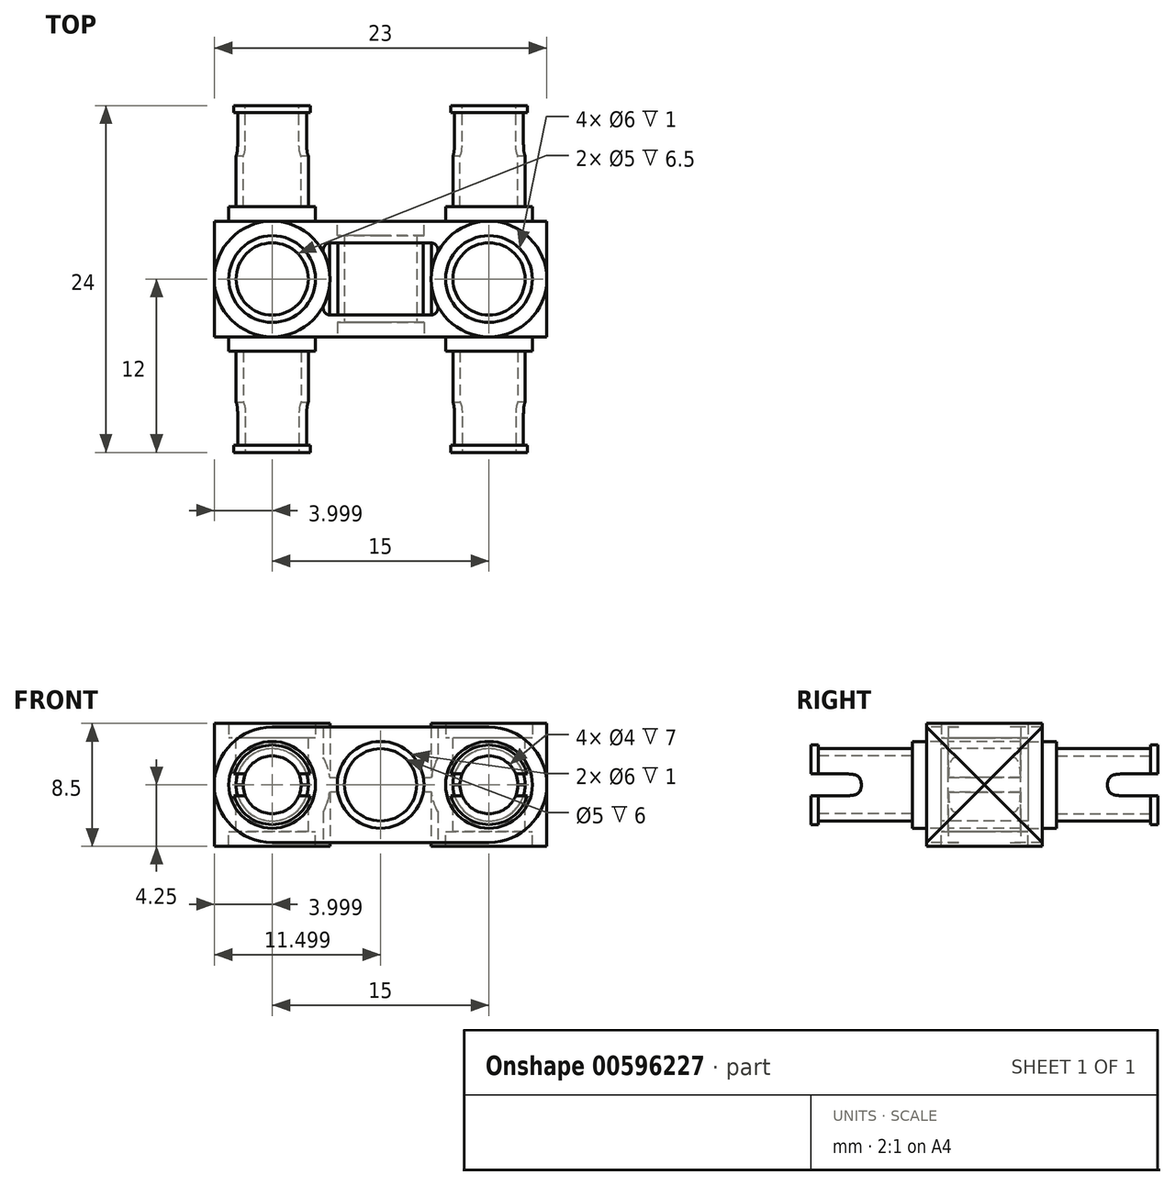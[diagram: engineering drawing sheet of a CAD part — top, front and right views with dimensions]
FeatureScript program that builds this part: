
annotation { "Feature Type Name" : "Feature", "Feature Type Description" : "" }
export const myFeature = defineFeature(function(context is Context, id is Id, definition is map)
    precondition{}
    {
        {
            var Q0;
            Q0=qCreatedBy(makeId("Top.planeOp"),FACE);
            var sketch = newSketch(context, id + "F0", { "sketchPlane" : qUnion([Q0])});
            skArc(sketch, "E0", {"start": v(-16.77, -19.7) * mm, "mid": v(-17.2, -21.48) * mm, "end": v(-16.77, -23.26) * mm});
            skArc(sketch, "E1", {"start": v(-24.6, -23.26) * mm, "mid": v(-24.2, -21.48) * mm, "end": v(-24.6, -19.7) * mm});
            skLineSegment(sketch, "E2", {"start": v(-28.2, -25.48) * mm, "end": v(-13.2, -25.48) * mm});
            skLineSegment(sketch, "E3", {"start": v(-28.2, -17.48) * mm, "end": v(-13.2, -17.48) * mm});
            skLineSegment(sketch, "E4", {"start": v(-17.22, -23.98) * mm, "end": v(-24.16, -23.98) * mm});
            skLineSegment(sketch, "E5", {"start": v(-17.22, -18.98) * mm, "end": v(-24.16, -18.98) * mm});
            skArc(sketch, "E6.trimOffspring", {"start": v(-28.2, -17.48) * mm, "mid": v(-32.2, -21.48) * mm, "end": v(-28.2, -25.48) * mm});
            skArc(sketch, "E7.trimOffspring", {"start": v(-13.2, -25.48) * mm, "mid": v(-9.2, -21.48) * mm, "end": v(-13.2, -17.48) * mm});
            skPoint(sketch, "E8.visualSharp", {"position": v(-25.07, -23.98) * mm});
            skArc(sketch, "E8.filletArc", {"start": v(-24.6, -23.26) * mm, "mid": v(-24.58, -23.74) * mm, "end": v(-24.16, -23.98) * mm});
            skPoint(sketch, "E9.visualSharp", {"position": v(-16.31, -23.98) * mm});
            skArc(sketch, "E9.filletArc", {"start": v(-17.22, -23.98) * mm, "mid": v(-16.8, -23.74) * mm, "end": v(-16.77, -23.26) * mm});
            skPoint(sketch, "E10.visualSharp", {"position": v(-16.31, -18.98) * mm});
            skArc(sketch, "E10.filletArc", {"start": v(-16.77, -19.7) * mm, "mid": v(-16.8, -19.22) * mm, "end": v(-17.22, -18.98) * mm});
            skPoint(sketch, "E11.visualSharp", {"position": v(-25.07, -18.98) * mm});
            skArc(sketch, "E11.filletArc", {"start": v(-24.16, -18.98) * mm, "mid": v(-24.58, -19.22) * mm, "end": v(-24.6, -19.7) * mm});
            skSolve(sketch);
        }
        {
            var Q0;
            Q0=makeQuery(id+"F0.imprint","IMPRINT",FACE,{"disambiguationData":[TD([[makeQuery(id+"F0.imprint","IMPRINT",EDGE,{"derivedFrom":sQuery(id+"F0.wireOp",EDGE,"E1")}),1.0]])]});
            var Q1;
            Q1=makeQuery(id+"F0.imprint","IMPRINT",FACE,{"disambiguationData":[TD([[makeQuery(id+"F0.imprint","IMPRINT",EDGE,{"derivedFrom":sQuery(id+"F0.wireOp",EDGE,"E0")}),1.0]])]});
            var Q2;
            {var subQ0=sQuery(id+"F0.wireOp",EDGE,"E2");Q2=makeQuery(id+"F0.imprint","IMPRINT",FACE,{"disambiguationData":[TD([[makeQuery(id+"F0.imprint","IMPRINT",EDGE,{"derivedFrom":subQ0}),1.0]])]});}
            var Q3;
            {var subQ0=sQuery(id+"F0.wireOp",EDGE,"E3");Q3=makeQuery(id+"F0.imprint","IMPRINT",FACE,{"disambiguationData":[TD([[makeQuery(id+"F0.imprint","IMPRINT",EDGE,{"derivedFrom":subQ0}),-1.0]])]});}
            extrude(context, id + "F1", {"entities" : qUnion([Q0, Q1, Q2, Q3]), "depth" : 8 * mm, "offsetDistance" : 25 * mm});
        }
        {
            var Q0;
            Q0=makeQuery(id+"F1.opExtrude","SWEPT_FACE",FACE,{"disambiguationData":[OSD([sQuery(id+"F0.wireOp",EDGE,"E2")])]});
            var sketch = newSketch(context, id + "F2", { "sketchPlane" : qUnion([Q0])});
            skPoint(sketch, "E12.endSnap0", {"position": v(-13.2, 4) * mm});
            skCircle(sketch, "E13", {"center": v(-20.7, 4) * mm, "radius": 3 * mm});
            skCircle(sketch, "E14", {"center": v(-20.7, 4) * mm, "radius": 2.5 * mm});
            skSolve(sketch);
        }
        {
            var Q0;
            Q0=makeQuery(id+"F2.imprint","IMPRINT",FACE,{"disambiguationData":[TD([[makeQuery(id+"F2.imprint","IMPRINT",EDGE,{"derivedFrom":sQuery(id+"F2.wireOp",EDGE,"E13")}),1.0]])]});
            extrude(context, id + "F3", {"entities" : qUnion([Q0]), "operationType" : NewBodyOperationType.ADD, "oppositeDirection" : true, "depth" : 8 * mm, "offsetDistance" : 25 * mm});
        }
        {
            var Q0;
            Q0=makeQuery(id+"F2.imprint","IMPRINT",FACE,{"disambiguationData":[TD([[makeQuery(id+"F2.imprint","IMPRINT",EDGE,{"derivedFrom":sQuery(id+"F2.wireOp",EDGE,"E14")}),1.0]])]});
            extrude(context, id + "F4", {"entities" : qUnion([Q0]), "operationType" : NewBodyOperationType.REMOVE, "oppositeDirection" : true, "depth" : 25 * mm, "offsetDistance" : 25 * mm});
        }
        {
            var Q0;
            Q0=makeQuery(id+"F2.imprint","IMPRINT",FACE,{"disambiguationData":[TD([[makeQuery(id+"F2.imprint","IMPRINT",EDGE,{"derivedFrom":sQuery(id+"F2.wireOp",EDGE,"E13")}),1.0]])]});
            extrude(context, id + "F5", {"entities" : qUnion([Q0]), "operationType" : NewBodyOperationType.REMOVE, "oppositeDirection" : true, "depth" : 1 * mm, "offsetDistance" : 25 * mm});
        }
        {
            var Q0;
            Q0=makeQuery(id+"F1.opExtrude","SWEPT_FACE",FACE,{"disambiguationData":[OSD([sQuery(id+"F0.wireOp",EDGE,"E3")])]});
            var sketch = newSketch(context, id + "F6", { "sketchPlane" : qUnion([Q0])});
            skCircle(sketch, "E15", {"center": v(20.7, 4) * mm, "radius": 3 * mm});
            skSolve(sketch);
        }
        {
            var Q0;
            Q0=makeQuery(id+"F6.imprint","IMPRINT",FACE,{"disambiguationData":[TD([[makeQuery(id+"F6.imprint","IMPRINT",EDGE,{"derivedFrom":sQuery(id+"F6.wireOp",EDGE,"E15")}),1.0]])]});
            extrude(context, id + "F7", {"entities" : qUnion([Q0]), "operationType" : NewBodyOperationType.REMOVE, "oppositeDirection" : true, "depth" : 1 * mm, "offsetDistance" : 25 * mm});
        }
        {
            var Q0;
            Q0=makeQuery(id+"F1.opExtrude","SWEPT_FACE",FACE,{"disambiguationData":[OSD([sQuery(id+"F0.wireOp",EDGE,"E3")])]});
            var sketch = newSketch(context, id + "F8", { "sketchPlane" : qUnion([Q0])});
            skCircle(sketch, "E16", {"center": v(13.2, 4) * mm, "radius": 4 * mm});
            skCircle(sketch, "E17", {"center": v(28.2, 4) * mm, "radius": 4 * mm});
            skSolve(sketch);
        }
        {
            var Q0;
            {var subQ1=sQuery(id+"F0.wireOp",EDGE,"E3");var subQ2=makeQuery(id+"F1.opExtrude","SWEPT_EDGE",EDGE,{"disambiguationData":[OSD([subQ1,sQuery(id+"F0.wireOp",EDGE,"E7.trimOffspring")])]});Q0=makeQuery(id+"F8.imprint","IMPRINT",FACE,{"disambiguationData":[TD([[makeQuery(id+"F8.imprint","IMPRINT",EDGE,{"derivedFrom":subQ2}),1.0]])]});}
            var Q1;
            {var subQ1=sQuery(id+"F0.wireOp",EDGE,"E3");var subQ2=makeQuery(id+"F1.opExtrude","SWEPT_EDGE",EDGE,{"disambiguationData":[OSD([subQ1,sQuery(id+"F0.wireOp",EDGE,"E7.trimOffspring")])]});Q1=makeQuery(id+"F8.imprint","IMPRINT",FACE,{"disambiguationData":[TD([[makeQuery(id+"F8.imprint","IMPRINT",EDGE,{"derivedFrom":subQ2}),-1.0]])]});}
            var Q2;
            {var subQ1=sQuery(id+"F0.wireOp",EDGE,"E3");var subQ2=makeQuery(id+"F1.opExtrude","SWEPT_EDGE",EDGE,{"disambiguationData":[OSD([subQ1,sQuery(id+"F0.wireOp",EDGE,"E6.trimOffspring")])]});Q2=makeQuery(id+"F8.imprint","IMPRINT",FACE,{"disambiguationData":[TD([[makeQuery(id+"F8.imprint","IMPRINT",EDGE,{"derivedFrom":subQ2}),-1.0]])]});}
            var Q3;
            {var subQ1=sQuery(id+"F0.wireOp",EDGE,"E3");var subQ2=makeQuery(id+"F1.opExtrude","SWEPT_EDGE",EDGE,{"disambiguationData":[OSD([subQ1,sQuery(id+"F0.wireOp",EDGE,"E6.trimOffspring")])]});Q3=makeQuery(id+"F8.imprint","IMPRINT",FACE,{"disambiguationData":[TD([[makeQuery(id+"F8.imprint","IMPRINT",EDGE,{"derivedFrom":subQ2}),1.0]])]});}
            extrude(context, id + "F9", {"entities" : qUnion([Q0, Q1, Q2, Q3]), "operationType" : NewBodyOperationType.ADD, "oppositeDirection" : true, "depth" : 16 * mm, "offsetDistance" : 25 * mm});
        }
        {
            var Q0;
            {var subQ1=sQuery(id+"F0.wireOp",EDGE,"E3");var subQ2=makeQuery(id+"F1.opExtrude","SWEPT_EDGE",EDGE,{"disambiguationData":[OSD([subQ1,sQuery(id+"F0.wireOp",EDGE,"E7.trimOffspring")])]});Q0=makeQuery(id+"F8.imprint","IMPRINT",FACE,{"disambiguationData":[TD([[makeQuery(id+"F8.imprint","IMPRINT",EDGE,{"derivedFrom":subQ2}),1.0]])]});}
            var Q1;
            {var subQ1=sQuery(id+"F0.wireOp",EDGE,"E3");var subQ2=makeQuery(id+"F1.opExtrude","SWEPT_EDGE",EDGE,{"disambiguationData":[OSD([subQ1,sQuery(id+"F0.wireOp",EDGE,"E7.trimOffspring")])]});Q1=makeQuery(id+"F8.imprint","IMPRINT",FACE,{"disambiguationData":[TD([[makeQuery(id+"F8.imprint","IMPRINT",EDGE,{"derivedFrom":subQ2}),-1.0]])]});}
            var Q2;
            {var subQ1=sQuery(id+"F0.wireOp",EDGE,"E3");var subQ2=makeQuery(id+"F1.opExtrude","SWEPT_EDGE",EDGE,{"disambiguationData":[OSD([subQ1,sQuery(id+"F0.wireOp",EDGE,"E6.trimOffspring")])]});Q2=makeQuery(id+"F8.imprint","IMPRINT",FACE,{"disambiguationData":[TD([[makeQuery(id+"F8.imprint","IMPRINT",EDGE,{"derivedFrom":subQ2}),-1.0]])]});}
            var Q3;
            {var subQ1=sQuery(id+"F0.wireOp",EDGE,"E3");var subQ2=makeQuery(id+"F1.opExtrude","SWEPT_EDGE",EDGE,{"disambiguationData":[OSD([subQ1,sQuery(id+"F0.wireOp",EDGE,"E6.trimOffspring")])]});Q3=makeQuery(id+"F8.imprint","IMPRINT",FACE,{"disambiguationData":[TD([[makeQuery(id+"F8.imprint","IMPRINT",EDGE,{"derivedFrom":subQ2}),1.0]])]});}
            extrude(context, id + "F10", {"entities" : qUnion([Q0, Q1, Q2, Q3]), "operationType" : NewBodyOperationType.ADD, "depth" : 8 * mm, "offsetDistance" : 25 * mm});
        }
        {
            var Q0;
            Q0=makeQuery(id+"F10.opExtrude","CAP_FACE",FACE,{"disambiguationData":[OSD([sQuery(id+"F8.wireOp",EDGE,"E16")])],"isStart":false});
            var sketch = newSketch(context, id + "F11", { "sketchPlane" : qUnion([Q0])});
            skCircle(sketch, "E18", {"center": v(13.2, 4) * mm, "radius": 3 * mm});
            skCircle(sketch, "E19", {"center": v(13.2, 4) * mm, "radius": 2.5 * mm});
            skSolve(sketch);
        }
        {
            var Q0;
            Q0=makeQuery(id+"F11.imprint","IMPRINT",FACE,{"disambiguationData":[TD([[makeQuery(id+"F11.imprint","IMPRINT",EDGE,{"derivedFrom":sQuery(id+"F11.wireOp",EDGE,"E18")}),-1.0]])]});
            extrude(context, id + "F12", {"entities" : qUnion([Q0]), "operationType" : NewBodyOperationType.REMOVE, "oppositeDirection" : true, "depth" : 8 * mm, "offsetDistance" : 25 * mm});
        }
        {
            var Q0;
            Q0=makeQuery(id+"F11.imprint","IMPRINT",FACE,{"disambiguationData":[TD([[makeQuery(id+"F11.imprint","IMPRINT",EDGE,{"derivedFrom":sQuery(id+"F11.wireOp",EDGE,"E18")}),1.0]])]});
            extrude(context, id + "F13", {"entities" : qUnion([Q0]), "operationType" : NewBodyOperationType.REMOVE, "oppositeDirection" : true, "depth" : 7 * mm, "offsetDistance" : 25 * mm});
        }
        {
            var Q0;
            Q0=makeQuery(id+"F10.opExtrude","CAP_FACE",FACE,{"disambiguationData":[OSD([sQuery(id+"F8.wireOp",EDGE,"E16")])],"isStart":false});
            var sketch = newSketch(context, id + "F14", { "sketchPlane" : qUnion([Q0])});
            skCircle(sketch, "E20", {"center": v(13.2, 4) * mm, "radius": 2.75 * mm});
            skSolve(sketch);
        }
        {
            var Q0;
            Q0=makeQuery(id+"F14.imprint","IMPRINT",FACE,{"disambiguationData":[TD([[makeQuery(id+"F14.imprint","IMPRINT",EDGE,{"derivedFrom":sQuery(id+"F14.wireOp",EDGE,"E20")}),1.0]])]});
            extrude(context, id + "F15", {"entities" : qUnion([Q0]), "operationType" : NewBodyOperationType.ADD, "oppositeDirection" : true, "depth" : .5 * mm, "offsetDistance" : 25 * mm});
        }
        {
            var Q0;
            Q0=makeQuery(id+"F15.boolean.opBoolean","MERGE",FACE,{"derivedFrom":[makeQuery(id+"F10.opExtrude","CAP_FACE",FACE,{"disambiguationData":[OSD([sQuery(id+"F8.wireOp",EDGE,"E16")])],"isStart":false}),makeQuery(id+"F15.opExtrude","CAP_FACE",FACE,{"disambiguationData":[OSD([sQuery(id+"F11.wireOp",EDGE,"E19"),sQuery(id+"F14.wireOp",EDGE,"E20")])],"isStart":true})]});
            var sketch = newSketch(context, id + "F16", { "sketchPlane" : qUnion([Q0])});
            skCircle(sketch, "E21", {"center": v(13.2, 4) * mm, "radius": 2 * mm});
            skSolve(sketch);
        }
        {
            var Q0;
            Q0=makeQuery(id+"F16.imprint","IMPRINT",FACE,{"disambiguationData":[TD([[makeQuery(id+"F16.imprint","IMPRINT",EDGE,{"derivedFrom":sQuery(id+"F16.wireOp",EDGE,"E21")}),1.0]])]});
            extrude(context, id + "F17", {"entities" : qUnion([Q0]), "operationType" : NewBodyOperationType.REMOVE, "oppositeDirection" : true, "depth" : 7 * mm, "offsetDistance" : 25 * mm});
        }
        {
            var Q0;
            Q0=makeQuery(id+"F10.opExtrude","CAP_FACE",FACE,{"disambiguationData":[OSD([sQuery(id+"F8.wireOp",EDGE,"E17")])],"isStart":false});
            var sketch = newSketch(context, id + "F18", { "sketchPlane" : qUnion([Q0])});
            skCircle(sketch, "E22", {"center": v(28.2, 4) * mm, "radius": 3 * mm});
            skCircle(sketch, "E23", {"center": v(28.2, 4) * mm, "radius": 2.5 * mm});
            skCircle(sketch, "E24", {"center": v(28.2, 4) * mm, "radius": 2 * mm});
            skSolve(sketch);
        }
        {
            var Q0;
            Q0=makeQuery(id+"F18.imprint","IMPRINT",FACE,{"disambiguationData":[TD([[makeQuery(id+"F18.imprint","IMPRINT",EDGE,{"derivedFrom":sQuery(id+"F18.wireOp",EDGE,"E22")}),-1.0]])]});
            extrude(context, id + "F19", {"entities" : qUnion([Q0]), "operationType" : NewBodyOperationType.REMOVE, "oppositeDirection" : true, "depth" : 8 * mm, "offsetDistance" : 25 * mm});
        }
        {
            var Q0;
            Q0=makeQuery(id+"F18.imprint","IMPRINT",FACE,{"disambiguationData":[TD([[makeQuery(id+"F18.imprint","IMPRINT",EDGE,{"derivedFrom":sQuery(id+"F18.wireOp",EDGE,"E22")}),1.0]])]});
            extrude(context, id + "F20", {"entities" : qUnion([Q0]), "operationType" : NewBodyOperationType.REMOVE, "oppositeDirection" : true, "depth" : 7 * mm, "offsetDistance" : 25 * mm});
        }
        {
            var Q0;
            Q0=makeQuery(id+"F18.imprint","IMPRINT",FACE,{"disambiguationData":[TD([[makeQuery(id+"F18.imprint","IMPRINT",EDGE,{"derivedFrom":sQuery(id+"F18.wireOp",EDGE,"E24")}),1.0]])]});
            extrude(context, id + "F21", {"entities" : qUnion([Q0]), "operationType" : NewBodyOperationType.REMOVE, "oppositeDirection" : true, "depth" : 7 * mm, "offsetDistance" : 25 * mm});
        }
        {
            var Q0;
            Q0=makeQuery(id+"F10.opExtrude","CAP_FACE",FACE,{"disambiguationData":[OSD([sQuery(id+"F8.wireOp",EDGE,"E17")])],"isStart":false});
            var sketch = newSketch(context, id + "F22", { "sketchPlane" : qUnion([Q0])});
            skCircle(sketch, "E25", {"center": v(28.2, 4) * mm, "radius": 2.75 * mm});
            skSolve(sketch);
        }
        {
            var Q0;
            Q0=makeQuery(id+"F22.imprint","IMPRINT",FACE,{"disambiguationData":[TD([[makeQuery(id+"F22.imprint","IMPRINT",EDGE,{"derivedFrom":sQuery(id+"F22.wireOp",EDGE,"E25")}),1.0]])]});
            extrude(context, id + "F23", {"entities" : qUnion([Q0]), "operationType" : NewBodyOperationType.ADD, "oppositeDirection" : true, "depth" : .5 * mm, "offsetDistance" : 25 * mm});
        }
        {
            var Q0;
            Q0=makeQuery(id+"F23.boolean.opBoolean","MERGE",FACE,{"derivedFrom":[makeQuery(id+"F10.opExtrude","CAP_FACE",FACE,{"disambiguationData":[OSD([sQuery(id+"F8.wireOp",EDGE,"E17")])],"isStart":false}),makeQuery(id+"F23.opExtrude","CAP_FACE",FACE,{"disambiguationData":[OSD([sQuery(id+"F18.wireOp",EDGE,"E23"),sQuery(id+"F22.wireOp",EDGE,"E25")])],"isStart":true})]});
            var sketch = newSketch(context, id + "F24", { "sketchPlane" : qUnion([Q0])});
            skLineSegment(sketch, "E26", {"start": v(13.2, 4) * mm, "end": v(13.2, 4.75) * mm});
            skLineSegment(sketch, "E27", {"start": v(13.2, 4.75) * mm, "end": v(36.7, 4.75) * mm});
            skLineSegment(sketch, "E28", {"start": v(36.7, 4.75) * mm, "end": v(36.7, 3.25) * mm});
            skLineSegment(sketch, "E29", {"start": v(36.7, 3.25) * mm, "end": v(7.51, 3.25) * mm});
            skLineSegment(sketch, "E30", {"start": v(7.51, 3.25) * mm, "end": v(7.51, 4.75) * mm});
            skLineSegment(sketch, "E31", {"start": v(7.51, 4.75) * mm, "end": v(13.2, 4.75) * mm});
            skSolve(sketch);
        }
        {
            var Q0;
            {var subQ1=sQuery(id+"F24.wireOp",EDGE,"E30");Q0=makeQuery(id+"F24.imprint","IMPRINT",FACE,{"disambiguationData":[TD([[makeQuery(id+"F24.imprint","IMPRINT",EDGE,{"derivedFrom":subQ1}),-1.0]])]});}
            var Q1;
            {var subQ0=sQuery(id+"F24.wireOp",EDGE,"E27");var subQ1=makeQuery(id+"F23.opExtrude","CAP_EDGE",EDGE,{"disambiguationData":[OSD([sQuery(id+"F22.wireOp",EDGE,"E25")])],"isStart":true});var subQ2=makeQuery(id+"F24.imprint","INTERSECT",VERTEX,{"disambiguationData":[OD(1.0)],"derivedFrom":[subQ1,subQ0]});Q1=makeQuery(id+"F24.imprint","IMPRINT",FACE,{"disambiguationData":[TD([[makeQuery(id+"F24.imprint","IMPRINT",EDGE,{"disambiguationData":[TD([[subQ2,1.0]])],"derivedFrom":subQ0}),-1.0]])]});}
            var Q2;
            {var subQ0=sQuery(id+"F24.wireOp",EDGE,"E27");var subQ1=makeQuery(id+"F23.opExtrude","CAP_EDGE",EDGE,{"disambiguationData":[OSD([sQuery(id+"F22.wireOp",EDGE,"E25")])],"isStart":true});var subQ2=makeQuery(id+"F24.imprint","INTERSECT",VERTEX,{"disambiguationData":[OD(0.0)],"derivedFrom":[subQ1,subQ0]});Q2=makeQuery(id+"F24.imprint","IMPRINT",FACE,{"disambiguationData":[TD([[makeQuery(id+"F24.imprint","IMPRINT",EDGE,{"disambiguationData":[TD([[subQ2,-1.0]])],"derivedFrom":subQ0}),-1.0]])]});}
            extrude(context, id + "F25", {"entities" : qUnion([Q0, Q1, Q2]), "operationType" : NewBodyOperationType.REMOVE, "oppositeDirection" : true, "depth" : 3.5 * mm, "offsetDistance" : 25 * mm});
        }
        {
            var Q0;
            {var subQ0=sQuery(id+"F24.wireOp",EDGE,"E31");var subQ1=sQuery(id+"F24.wireOp",EDGE,"E27");Q0=makeQuery(id+"F25.boolean.opBoolean","COPY",EDGE,{"disambiguationData":[TD([makeQuery(id+"F13.boolean.opBoolean","COPY",FACE,{"derivedFrom":makeQuery(id+"F13.opExtrude","SWEPT_FACE",FACE,{"disambiguationData":[OSD([sQuery(id+"F11.wireOp",EDGE,"E19")])]})}),makeQuery(id+"F17.boolean.opBoolean","COPY",FACE,{"derivedFrom":makeQuery(id+"F17.opExtrude","SWEPT_FACE",FACE,{"disambiguationData":[OSD([sQuery(id+"F16.wireOp",EDGE,"E21")])]})}),makeQuery(id+"F25.opExtrude","CAP_FACE",FACE,{"disambiguationData":[OSD([sQuery(id+"F18.wireOp",EDGE,"E24"),subQ1,sQuery(id+"F24.wireOp",EDGE,"E29"),sQuery(id+"F24.wireOp",EDGE,"E30"),subQ0])],"isStart":false}),makeQuery(id+"F25.opExtrude","SWEPT_FACE",FACE,{"disambiguationData":[OSD([subQ1,subQ0])]})]),OD(1.0)],"derivedFrom":makeQuery(id+"F25.opExtrude","CAP_EDGE",EDGE,{"disambiguationData":[OSD([subQ1,subQ0])],"isStart":false})});}
            var Q1;
            {var subQ0=sQuery(id+"F24.wireOp",EDGE,"E30");var subQ1=sQuery(id+"F24.wireOp",EDGE,"E29");var subQ2=sQuery(id+"F18.wireOp",EDGE,"E24");var subQ3=makeQuery(id+"F24.imprint","INTERSECT",VERTEX,{"disambiguationData":[OD(1.0)],"derivedFrom":[makeQuery(id+"F23.opExtrude","CAP_EDGE",EDGE,{"disambiguationData":[OSD([sQuery(id+"F22.wireOp",EDGE,"E25")])],"isStart":true}),subQ1]});var subQ4=makeQuery(id+"F24.imprint","IMPRINT",EDGE,{"disambiguationData":[TD([[makeQuery(id+"F24.imprint","INTERSECT",VERTEX,{"derivedFrom":[subQ1,subQ0]}),1.0]])],"derivedFrom":subQ1});var subQ5=makeQuery(id+"F24.imprint","IMPRINT",EDGE,{"disambiguationData":[TD([[subQ3,1.0]])],"derivedFrom":subQ1});Q1=makeQuery(id+"F25.boolean.opBoolean","COPY",EDGE,{"disambiguationData":[TD([makeQuery(id+"F13.boolean.opBoolean","COPY",FACE,{"derivedFrom":makeQuery(id+"F13.opExtrude","SWEPT_FACE",FACE,{"disambiguationData":[OSD([sQuery(id+"F11.wireOp",EDGE,"E19")])]})}),makeQuery(id+"F17.boolean.opBoolean","COPY",FACE,{"derivedFrom":makeQuery(id+"F17.opExtrude","SWEPT_FACE",FACE,{"disambiguationData":[OSD([sQuery(id+"F16.wireOp",EDGE,"E21")])]})}),makeQuery(id+"F25.opExtrude","CAP_FACE",FACE,{"disambiguationData":[OSD([subQ2,sQuery(id+"F24.wireOp",EDGE,"E27"),subQ1,subQ0,sQuery(id+"F24.wireOp",EDGE,"E31")])],"isStart":false}),makeQuery(id+"F25.opExtrude","SWEPT_FACE",FACE,{"disambiguationData":[OSD([subQ1]),TDD([subQ5,subQ4])]})]),OD(1.0)],"derivedFrom":makeQuery(id+"F25.opExtrude","CAP_EDGE",EDGE,{"disambiguationData":[OSD([subQ1]),TDD([subQ5,subQ4])],"isStart":false})});}
            var Q2;
            {var subQ0=sQuery(id+"F24.wireOp",EDGE,"E30");var subQ1=sQuery(id+"F24.wireOp",EDGE,"E29");var subQ2=sQuery(id+"F18.wireOp",EDGE,"E24");var subQ3=makeQuery(id+"F24.imprint","INTERSECT",VERTEX,{"disambiguationData":[OD(1.0)],"derivedFrom":[makeQuery(id+"F23.opExtrude","CAP_EDGE",EDGE,{"disambiguationData":[OSD([sQuery(id+"F22.wireOp",EDGE,"E25")])],"isStart":true}),subQ1]});var subQ4=makeQuery(id+"F24.imprint","IMPRINT",EDGE,{"disambiguationData":[TD([[makeQuery(id+"F24.imprint","INTERSECT",VERTEX,{"derivedFrom":[subQ1,subQ0]}),1.0]])],"derivedFrom":subQ1});var subQ5=makeQuery(id+"F24.imprint","IMPRINT",EDGE,{"disambiguationData":[TD([[subQ3,1.0]])],"derivedFrom":subQ1});Q2=makeQuery(id+"F25.boolean.opBoolean","COPY",EDGE,{"disambiguationData":[TD([makeQuery(id+"F13.boolean.opBoolean","COPY",FACE,{"derivedFrom":makeQuery(id+"F13.opExtrude","SWEPT_FACE",FACE,{"disambiguationData":[OSD([sQuery(id+"F11.wireOp",EDGE,"E19")])]})}),makeQuery(id+"F17.boolean.opBoolean","COPY",FACE,{"derivedFrom":makeQuery(id+"F17.opExtrude","SWEPT_FACE",FACE,{"disambiguationData":[OSD([sQuery(id+"F16.wireOp",EDGE,"E21")])]})}),makeQuery(id+"F25.opExtrude","CAP_FACE",FACE,{"disambiguationData":[OSD([subQ2,sQuery(id+"F24.wireOp",EDGE,"E27"),subQ1,subQ0,sQuery(id+"F24.wireOp",EDGE,"E31")])],"isStart":false}),makeQuery(id+"F25.opExtrude","SWEPT_FACE",FACE,{"disambiguationData":[OSD([subQ1]),TDD([subQ5,subQ4])]})]),OD(0.0)],"derivedFrom":makeQuery(id+"F25.opExtrude","CAP_EDGE",EDGE,{"disambiguationData":[OSD([subQ1]),TDD([subQ5,subQ4])],"isStart":false})});}
            var Q3;
            {var subQ0=sQuery(id+"F24.wireOp",EDGE,"E31");var subQ1=sQuery(id+"F24.wireOp",EDGE,"E27");Q3=makeQuery(id+"F25.boolean.opBoolean","COPY",EDGE,{"disambiguationData":[TD([makeQuery(id+"F13.boolean.opBoolean","COPY",FACE,{"derivedFrom":makeQuery(id+"F13.opExtrude","SWEPT_FACE",FACE,{"disambiguationData":[OSD([sQuery(id+"F11.wireOp",EDGE,"E19")])]})}),makeQuery(id+"F17.boolean.opBoolean","COPY",FACE,{"derivedFrom":makeQuery(id+"F17.opExtrude","SWEPT_FACE",FACE,{"disambiguationData":[OSD([sQuery(id+"F16.wireOp",EDGE,"E21")])]})}),makeQuery(id+"F25.opExtrude","CAP_FACE",FACE,{"disambiguationData":[OSD([sQuery(id+"F18.wireOp",EDGE,"E24"),subQ1,sQuery(id+"F24.wireOp",EDGE,"E29"),sQuery(id+"F24.wireOp",EDGE,"E30"),subQ0])],"isStart":false}),makeQuery(id+"F25.opExtrude","SWEPT_FACE",FACE,{"disambiguationData":[OSD([subQ1,subQ0])]})]),OD(0.0)],"derivedFrom":makeQuery(id+"F25.opExtrude","CAP_EDGE",EDGE,{"disambiguationData":[OSD([subQ1,subQ0])],"isStart":false})});}
            var Q4;
            Q4=makeQuery(id+"F25.boolean.opBoolean","COPY",EDGE,{"derivedFrom":makeQuery(id+"F25.opExtrude","CAP_EDGE",EDGE,{"disambiguationData":[OSD([sQuery(id+"F24.wireOp",EDGE,"E27")])],"isStart":false})});
            var Q5;
            {var subQ0=sQuery(id+"F24.wireOp",EDGE,"E31");var subQ1=sQuery(id+"F24.wireOp",EDGE,"E27");var subQ2=sQuery(id+"F18.wireOp",EDGE,"E24");Q5=makeQuery(id+"F25.boolean.opBoolean","COPY",EDGE,{"disambiguationData":[TD([makeQuery(id+"F20.boolean.opBoolean","COPY",FACE,{"derivedFrom":makeQuery(id+"F20.opExtrude","SWEPT_FACE",FACE,{"disambiguationData":[OSD([sQuery(id+"F18.wireOp",EDGE,"E23")])]})}),makeQuery(id+"F21.boolean.opBoolean","COPY",FACE,{"derivedFrom":makeQuery(id+"F21.opExtrude","SWEPT_FACE",FACE,{"disambiguationData":[OSD([subQ2])]})}),makeQuery(id+"F25.opExtrude","CAP_FACE",FACE,{"disambiguationData":[OSD([subQ2,subQ1,sQuery(id+"F24.wireOp",EDGE,"E29"),sQuery(id+"F24.wireOp",EDGE,"E30"),subQ0])],"isStart":false}),makeQuery(id+"F25.opExtrude","SWEPT_FACE",FACE,{"disambiguationData":[OSD([subQ1,subQ0])]})])],"derivedFrom":makeQuery(id+"F25.opExtrude","CAP_EDGE",EDGE,{"disambiguationData":[OSD([subQ1,subQ0])],"isStart":false})});}
            var Q6;
            {var subQ0=sQuery(id+"F24.wireOp",EDGE,"E30");var subQ1=sQuery(id+"F24.wireOp",EDGE,"E29");var subQ2=makeQuery(id+"F24.imprint","INTERSECT",VERTEX,{"disambiguationData":[OD(1.0)],"derivedFrom":[makeQuery(id+"F23.opExtrude","CAP_EDGE",EDGE,{"disambiguationData":[OSD([sQuery(id+"F22.wireOp",EDGE,"E25")])],"isStart":true}),subQ1]});var subQ3=makeQuery(id+"F24.imprint","IMPRINT",EDGE,{"disambiguationData":[TD([[makeQuery(id+"F24.imprint","INTERSECT",VERTEX,{"derivedFrom":[subQ1,subQ0]}),1.0]])],"derivedFrom":subQ1});var subQ4=sQuery(id+"F18.wireOp",EDGE,"E24");var subQ5=makeQuery(id+"F24.imprint","IMPRINT",EDGE,{"disambiguationData":[TD([[subQ2,1.0]])],"derivedFrom":subQ1});Q6=makeQuery(id+"F25.boolean.opBoolean","COPY",EDGE,{"disambiguationData":[TD([makeQuery(id+"F20.boolean.opBoolean","COPY",FACE,{"derivedFrom":makeQuery(id+"F20.opExtrude","SWEPT_FACE",FACE,{"disambiguationData":[OSD([sQuery(id+"F18.wireOp",EDGE,"E23")])]})}),makeQuery(id+"F21.boolean.opBoolean","COPY",FACE,{"derivedFrom":makeQuery(id+"F21.opExtrude","SWEPT_FACE",FACE,{"disambiguationData":[OSD([subQ4])]})}),makeQuery(id+"F25.opExtrude","CAP_FACE",FACE,{"disambiguationData":[OSD([subQ4,sQuery(id+"F24.wireOp",EDGE,"E27"),subQ1,subQ0,sQuery(id+"F24.wireOp",EDGE,"E31")])],"isStart":false}),makeQuery(id+"F25.opExtrude","SWEPT_FACE",FACE,{"disambiguationData":[OSD([subQ1]),TDD([subQ5,subQ3])]})])],"derivedFrom":makeQuery(id+"F25.opExtrude","CAP_EDGE",EDGE,{"disambiguationData":[OSD([subQ1]),TDD([subQ5,subQ3])],"isStart":false})});}
            var Q7;
            {var subQ0=sQuery(id+"F24.wireOp",EDGE,"E29");Q7=makeQuery(id+"F25.boolean.opBoolean","COPY",EDGE,{"derivedFrom":makeQuery(id+"F25.opExtrude","CAP_EDGE",EDGE,{"disambiguationData":[OSD([subQ0]),TDD([makeQuery(id+"F24.imprint","IMPRINT",EDGE,{"disambiguationData":[TD([[makeQuery(id+"F24.imprint","INTERSECT",VERTEX,{"disambiguationData":[OD(0.0)],"derivedFrom":[makeQuery(id+"F23.opExtrude","CAP_EDGE",EDGE,{"disambiguationData":[OSD([sQuery(id+"F22.wireOp",EDGE,"E25")])],"isStart":true}),subQ0]}),-1.0]])],"derivedFrom":subQ0})])],"isStart":false})});}
            fillet(context, id + "F26", {"entities" : qUnion([Q0, Q1, Q2, Q3, Q4, Q5, Q6, Q7]), "radius" : 1 * mm, "tangentPropagation" : true, "rho" : .6, "crossSection" : FilletCrossSection.CONIC, "allowEdgeOverflow" : false});
        }
        {
            var Q0;
            Q0=makeQuery(id+"F9.opExtrude","CAP_FACE",FACE,{"disambiguationData":[OSD([sQuery(id+"F8.wireOp",EDGE,"E17")])],"isStart":false});
            var sketch = newSketch(context, id + "F27", { "sketchPlane" : qUnion([Q0])});
            skCircle(sketch, "E32", {"center": v(-28.2, 4) * mm, "radius": 3 * mm});
            skCircle(sketch, "E33", {"center": v(-28.2, 4) * mm, "radius": 2.5 * mm});
            skCircle(sketch, "E34", {"center": v(-28.2, 4) * mm, "radius": 2.75 * mm});
            skCircle(sketch, "E35", {"center": v(-28.2, 4) * mm, "radius": 2 * mm});
            skSolve(sketch);
        }
        {
            var Q0;
            Q0=makeQuery(id+"F27.imprint","IMPRINT",FACE,{"disambiguationData":[TD([[makeQuery(id+"F27.imprint","IMPRINT",EDGE,{"derivedFrom":sQuery(id+"F27.wireOp",EDGE,"E32")}),-1.0]])]});
            extrude(context, id + "F28", {"entities" : qUnion([Q0]), "operationType" : NewBodyOperationType.REMOVE, "oppositeDirection" : true, "depth" : 8 * mm, "offsetDistance" : 25 * mm});
        }
        {
            var Q0;
            Q0=makeQuery(id+"F27.imprint","IMPRINT",FACE,{"disambiguationData":[TD([[makeQuery(id+"F27.imprint","IMPRINT",EDGE,{"derivedFrom":sQuery(id+"F27.wireOp",EDGE,"E33")}),-1.0]])]});
            var Q1;
            Q1=makeQuery(id+"F27.imprint","IMPRINT",FACE,{"disambiguationData":[TD([[makeQuery(id+"F27.imprint","IMPRINT",EDGE,{"derivedFrom":sQuery(id+"F27.wireOp",EDGE,"E32")}),1.0]])]});
            extrude(context, id + "F29", {"entities" : qUnion([Q0, Q1]), "operationType" : NewBodyOperationType.REMOVE, "oppositeDirection" : true, "depth" : 7 * mm, "offsetDistance" : 25 * mm});
        }
        {
            var Q0;
            Q0=makeQuery(id+"F27.imprint","IMPRINT",FACE,{"disambiguationData":[TD([[makeQuery(id+"F27.imprint","IMPRINT",EDGE,{"derivedFrom":sQuery(id+"F27.wireOp",EDGE,"E33")}),-1.0]])]});
            extrude(context, id + "F30", {"entities" : qUnion([Q0]), "operationType" : NewBodyOperationType.ADD, "oppositeDirection" : true, "depth" : .5 * mm, "offsetDistance" : 25 * mm});
        }
        {
            var Q0;
            Q0=makeQuery(id+"F27.imprint","IMPRINT",FACE,{"disambiguationData":[TD([[makeQuery(id+"F27.imprint","IMPRINT",EDGE,{"derivedFrom":sQuery(id+"F27.wireOp",EDGE,"E35")}),1.0]])]});
            extrude(context, id + "F31", {"entities" : qUnion([Q0]), "operationType" : NewBodyOperationType.REMOVE, "oppositeDirection" : true, "depth" : 7 * mm, "offsetDistance" : 25 * mm});
        }
        {
            var Q0;
            Q0=makeQuery(id+"F9.opExtrude","CAP_FACE",FACE,{"disambiguationData":[OSD([sQuery(id+"F8.wireOp",EDGE,"E16")])],"isStart":false});
            var sketch = newSketch(context, id + "F32", { "sketchPlane" : qUnion([Q0])});
            skCircle(sketch, "E36", {"center": v(-13.2, 4) * mm, "radius": 3 * mm});
            skCircle(sketch, "E37", {"center": v(-13.2, 4) * mm, "radius": 2.5 * mm});
            skCircle(sketch, "E38", {"center": v(-13.2, 4) * mm, "radius": 2 * mm});
            skSolve(sketch);
        }
        {
            var Q0;
            Q0=makeQuery(id+"F32.imprint","IMPRINT",FACE,{"disambiguationData":[TD([[makeQuery(id+"F32.imprint","IMPRINT",EDGE,{"derivedFrom":sQuery(id+"F32.wireOp",EDGE,"E36")}),-1.0]])]});
            extrude(context, id + "F33", {"entities" : qUnion([Q0]), "operationType" : NewBodyOperationType.REMOVE, "oppositeDirection" : true, "depth" : 8 * mm, "offsetDistance" : 25 * mm});
        }
        {
            var Q0;
            Q0=makeQuery(id+"F32.imprint","IMPRINT",FACE,{"disambiguationData":[TD([[makeQuery(id+"F32.imprint","IMPRINT",EDGE,{"derivedFrom":sQuery(id+"F32.wireOp",EDGE,"E36")}),1.0]])]});
            extrude(context, id + "F34", {"entities" : qUnion([Q0]), "operationType" : NewBodyOperationType.REMOVE, "oppositeDirection" : true, "depth" : 7 * mm, "offsetDistance" : 25 * mm});
        }
        {
            var Q0;
            Q0=makeQuery(id+"F32.imprint","IMPRINT",FACE,{"disambiguationData":[TD([[makeQuery(id+"F32.imprint","IMPRINT",EDGE,{"derivedFrom":sQuery(id+"F32.wireOp",EDGE,"E38")}),1.0]])]});
            extrude(context, id + "F35", {"entities" : qUnion([Q0]), "operationType" : NewBodyOperationType.REMOVE, "oppositeDirection" : true, "depth" : 7 * mm, "offsetDistance" : 25 * mm});
        }
        {
            var Q0;
            Q0=makeQuery(id+"F9.opExtrude","CAP_FACE",FACE,{"disambiguationData":[OSD([sQuery(id+"F8.wireOp",EDGE,"E16")])],"isStart":false});
            var sketch = newSketch(context, id + "F36", { "sketchPlane" : qUnion([Q0])});
            skCircle(sketch, "E39", {"center": v(-13.2, 4) * mm, "radius": 2.75 * mm});
            skSolve(sketch);
        }
        {
            var Q0;
            Q0=makeQuery(id+"F36.imprint","IMPRINT",FACE,{"disambiguationData":[TD([[makeQuery(id+"F36.imprint","IMPRINT",EDGE,{"derivedFrom":sQuery(id+"F36.wireOp",EDGE,"E39")}),1.0]])]});
            extrude(context, id + "F37", {"entities" : qUnion([Q0]), "operationType" : NewBodyOperationType.ADD, "oppositeDirection" : true, "depth" : .5 * mm, "offsetDistance" : 25 * mm});
        }
        {
            var Q0;
            Q0=makeQuery(id+"F37.boolean.opBoolean","MERGE",FACE,{"derivedFrom":[makeQuery(id+"F9.opExtrude","CAP_FACE",FACE,{"disambiguationData":[OSD([sQuery(id+"F8.wireOp",EDGE,"E16")])],"isStart":false}),makeQuery(id+"F37.opExtrude","CAP_FACE",FACE,{"disambiguationData":[OSD([sQuery(id+"F32.wireOp",EDGE,"E37"),sQuery(id+"F36.wireOp",EDGE,"E39")])],"isStart":true})]});
            var sketch = newSketch(context, id + "F38", { "sketchPlane" : qUnion([Q0])});
            skLineSegment(sketch, "E40", {"start": v(-13.2, 4) * mm, "end": v(-13.2, 4.75) * mm});
            skLineSegment(sketch, "E41", {"start": v(-13.2, 4.75) * mm, "end": v(-33.18, 4.75) * mm});
            skLineSegment(sketch, "E42", {"start": v(-33.18, 4.75) * mm, "end": v(-33.18, 3.25) * mm});
            skLineSegment(sketch, "E43", {"start": v(-33.18, 3.25) * mm, "end": v(-4.02, 3.25) * mm});
            skLineSegment(sketch, "E44", {"start": v(-4.02, 3.25) * mm, "end": v(-4.02, 4.75) * mm});
            skLineSegment(sketch, "E45", {"start": v(-4.02, 4.75) * mm, "end": v(-13.2, 4.75) * mm});
            skSolve(sketch);
        }
        {
            var Q0;
            {var subQ0=sQuery(id+"F38.wireOp",EDGE,"E41");var subQ1=makeQuery(id+"F37.opExtrude","CAP_EDGE",EDGE,{"disambiguationData":[OSD([sQuery(id+"F36.wireOp",EDGE,"E39")])],"isStart":true});var subQ2=makeQuery(id+"F38.imprint","INTERSECT",VERTEX,{"derivedFrom":[subQ1,subQ0]});Q0=makeQuery(id+"F38.imprint","IMPRINT",FACE,{"disambiguationData":[TD([[makeQuery(id+"F38.imprint","IMPRINT",EDGE,{"disambiguationData":[TD([[subQ2,1.0]])],"derivedFrom":subQ0}),1.0]])]});}
            var Q1;
            {var subQ0=sQuery(id+"F38.wireOp",EDGE,"E43");var subQ1=makeQuery(id+"F37.opExtrude","CAP_EDGE",EDGE,{"disambiguationData":[OSD([sQuery(id+"F36.wireOp",EDGE,"E39")])],"isStart":true});var subQ2=makeQuery(id+"F38.imprint","INTERSECT",VERTEX,{"disambiguationData":[OD(1.0)],"derivedFrom":[subQ1,subQ0]});Q1=makeQuery(id+"F38.imprint","IMPRINT",FACE,{"disambiguationData":[TD([[makeQuery(id+"F38.imprint","IMPRINT",EDGE,{"disambiguationData":[TD([[subQ2,1.0]])],"derivedFrom":subQ0}),1.0]])]});}
            var Q2;
            {var subQ0=sQuery(id+"F38.wireOp",EDGE,"E42");Q2=makeQuery(id+"F38.imprint","IMPRINT",FACE,{"disambiguationData":[TD([[makeQuery(id+"F38.imprint","IMPRINT",EDGE,{"derivedFrom":subQ0}),1.0]])]});}
            extrude(context, id + "F39", {"entities" : qUnion([Q0, Q1, Q2]), "operationType" : NewBodyOperationType.REMOVE, "oppositeDirection" : true, "depth" : 3.5 * mm, "offsetDistance" : 25 * mm});
        }
        {
            var Q0;
            {var subQ0=sQuery(id+"F38.wireOp",EDGE,"E41");Q0=makeQuery(id+"F39.boolean.opBoolean","COPY",EDGE,{"disambiguationData":[TD([makeQuery(id+"F29.boolean.opBoolean","COPY",FACE,{"derivedFrom":makeQuery(id+"F29.opExtrude","SWEPT_FACE",FACE,{"disambiguationData":[OSD([sQuery(id+"F27.wireOp",EDGE,"E33")])]})}),makeQuery(id+"F31.boolean.opBoolean","COPY",FACE,{"derivedFrom":makeQuery(id+"F31.opExtrude","SWEPT_FACE",FACE,{"disambiguationData":[OSD([sQuery(id+"F27.wireOp",EDGE,"E35")])]})}),makeQuery(id+"F39.opExtrude","SWEPT_FACE",FACE,{"disambiguationData":[OSD([subQ0])]}),makeQuery(id+"F39.opExtrude","CAP_FACE",FACE,{"disambiguationData":[OSD([sQuery(id+"F32.wireOp",EDGE,"E38"),subQ0,sQuery(id+"F38.wireOp",EDGE,"E42"),sQuery(id+"F38.wireOp",EDGE,"E43")])],"isStart":false})]),OD(0.0)],"derivedFrom":makeQuery(id+"F39.opExtrude","CAP_EDGE",EDGE,{"disambiguationData":[OSD([subQ0])],"isStart":false})});}
            var Q1;
            {var subQ0=sQuery(id+"F38.wireOp",EDGE,"E43");var subQ1=sQuery(id+"F38.wireOp",EDGE,"E42");var subQ2=sQuery(id+"F32.wireOp",EDGE,"E38");var subQ3=makeQuery(id+"F38.imprint","INTERSECT",VERTEX,{"disambiguationData":[OD(0.0)],"derivedFrom":[makeQuery(id+"F37.opExtrude","CAP_EDGE",EDGE,{"disambiguationData":[OSD([sQuery(id+"F36.wireOp",EDGE,"E39")])],"isStart":true}),subQ0]});var subQ4=makeQuery(id+"F38.imprint","IMPRINT",EDGE,{"disambiguationData":[TD([[subQ3,-1.0]])],"derivedFrom":subQ0});var subQ5=makeQuery(id+"F38.imprint","IMPRINT",EDGE,{"disambiguationData":[TD([[makeQuery(id+"F38.imprint","INTERSECT",VERTEX,{"derivedFrom":[subQ1,subQ0]}),-1.0]])],"derivedFrom":subQ0});Q1=makeQuery(id+"F39.boolean.opBoolean","COPY",EDGE,{"disambiguationData":[TD([makeQuery(id+"F29.boolean.opBoolean","COPY",FACE,{"derivedFrom":makeQuery(id+"F29.opExtrude","SWEPT_FACE",FACE,{"disambiguationData":[OSD([sQuery(id+"F27.wireOp",EDGE,"E33")])]})}),makeQuery(id+"F31.boolean.opBoolean","COPY",FACE,{"derivedFrom":makeQuery(id+"F31.opExtrude","SWEPT_FACE",FACE,{"disambiguationData":[OSD([sQuery(id+"F27.wireOp",EDGE,"E35")])]})}),makeQuery(id+"F39.opExtrude","CAP_FACE",FACE,{"disambiguationData":[OSD([subQ2,sQuery(id+"F38.wireOp",EDGE,"E41"),subQ1,subQ0])],"isStart":false}),makeQuery(id+"F39.opExtrude","SWEPT_FACE",FACE,{"disambiguationData":[OSD([subQ0]),TDD([subQ5,subQ4])]})]),OD(0.0)],"derivedFrom":makeQuery(id+"F39.opExtrude","CAP_EDGE",EDGE,{"disambiguationData":[OSD([subQ0]),TDD([subQ5,subQ4])],"isStart":false})});}
            var Q2;
            {var subQ0=sQuery(id+"F38.wireOp",EDGE,"E43");var subQ1=sQuery(id+"F38.wireOp",EDGE,"E42");var subQ2=sQuery(id+"F32.wireOp",EDGE,"E38");var subQ3=makeQuery(id+"F38.imprint","INTERSECT",VERTEX,{"disambiguationData":[OD(0.0)],"derivedFrom":[makeQuery(id+"F37.opExtrude","CAP_EDGE",EDGE,{"disambiguationData":[OSD([sQuery(id+"F36.wireOp",EDGE,"E39")])],"isStart":true}),subQ0]});var subQ4=makeQuery(id+"F38.imprint","IMPRINT",EDGE,{"disambiguationData":[TD([[subQ3,-1.0]])],"derivedFrom":subQ0});var subQ5=makeQuery(id+"F38.imprint","IMPRINT",EDGE,{"disambiguationData":[TD([[makeQuery(id+"F38.imprint","INTERSECT",VERTEX,{"derivedFrom":[subQ1,subQ0]}),-1.0]])],"derivedFrom":subQ0});Q2=makeQuery(id+"F39.boolean.opBoolean","COPY",EDGE,{"disambiguationData":[TD([makeQuery(id+"F29.boolean.opBoolean","COPY",FACE,{"derivedFrom":makeQuery(id+"F29.opExtrude","SWEPT_FACE",FACE,{"disambiguationData":[OSD([sQuery(id+"F27.wireOp",EDGE,"E33")])]})}),makeQuery(id+"F31.boolean.opBoolean","COPY",FACE,{"derivedFrom":makeQuery(id+"F31.opExtrude","SWEPT_FACE",FACE,{"disambiguationData":[OSD([sQuery(id+"F27.wireOp",EDGE,"E35")])]})}),makeQuery(id+"F39.opExtrude","CAP_FACE",FACE,{"disambiguationData":[OSD([subQ2,sQuery(id+"F38.wireOp",EDGE,"E41"),subQ1,subQ0])],"isStart":false}),makeQuery(id+"F39.opExtrude","SWEPT_FACE",FACE,{"disambiguationData":[OSD([subQ0]),TDD([subQ5,subQ4])]})]),OD(1.0)],"derivedFrom":makeQuery(id+"F39.opExtrude","CAP_EDGE",EDGE,{"disambiguationData":[OSD([subQ0]),TDD([subQ5,subQ4])],"isStart":false})});}
            var Q3;
            {var subQ0=sQuery(id+"F38.wireOp",EDGE,"E41");Q3=makeQuery(id+"F39.boolean.opBoolean","COPY",EDGE,{"disambiguationData":[TD([makeQuery(id+"F29.boolean.opBoolean","COPY",FACE,{"derivedFrom":makeQuery(id+"F29.opExtrude","SWEPT_FACE",FACE,{"disambiguationData":[OSD([sQuery(id+"F27.wireOp",EDGE,"E33")])]})}),makeQuery(id+"F31.boolean.opBoolean","COPY",FACE,{"derivedFrom":makeQuery(id+"F31.opExtrude","SWEPT_FACE",FACE,{"disambiguationData":[OSD([sQuery(id+"F27.wireOp",EDGE,"E35")])]})}),makeQuery(id+"F39.opExtrude","SWEPT_FACE",FACE,{"disambiguationData":[OSD([subQ0])]}),makeQuery(id+"F39.opExtrude","CAP_FACE",FACE,{"disambiguationData":[OSD([sQuery(id+"F32.wireOp",EDGE,"E38"),subQ0,sQuery(id+"F38.wireOp",EDGE,"E42"),sQuery(id+"F38.wireOp",EDGE,"E43")])],"isStart":false})]),OD(1.0)],"derivedFrom":makeQuery(id+"F39.opExtrude","CAP_EDGE",EDGE,{"disambiguationData":[OSD([subQ0])],"isStart":false})});}
            var Q4;
            {var subQ0=sQuery(id+"F38.wireOp",EDGE,"E41");var subQ1=sQuery(id+"F32.wireOp",EDGE,"E38");Q4=makeQuery(id+"F39.boolean.opBoolean","COPY",EDGE,{"disambiguationData":[TD([makeQuery(id+"F34.boolean.opBoolean","COPY",FACE,{"derivedFrom":makeQuery(id+"F34.opExtrude","SWEPT_FACE",FACE,{"disambiguationData":[OSD([sQuery(id+"F32.wireOp",EDGE,"E37")])]})}),makeQuery(id+"F35.boolean.opBoolean","COPY",FACE,{"derivedFrom":makeQuery(id+"F35.opExtrude","SWEPT_FACE",FACE,{"disambiguationData":[OSD([subQ1])]})}),makeQuery(id+"F39.opExtrude","SWEPT_FACE",FACE,{"disambiguationData":[OSD([subQ0])]}),makeQuery(id+"F39.opExtrude","CAP_FACE",FACE,{"disambiguationData":[OSD([subQ1,subQ0,sQuery(id+"F38.wireOp",EDGE,"E42"),sQuery(id+"F38.wireOp",EDGE,"E43")])],"isStart":false})])],"derivedFrom":makeQuery(id+"F39.opExtrude","CAP_EDGE",EDGE,{"disambiguationData":[OSD([subQ0])],"isStart":false})});}
            var Q5;
            Q5=makeQuery(id+"F39.boolean.opBoolean","COPY",EDGE,{"derivedFrom":makeQuery(id+"F39.opExtrude","CAP_EDGE",EDGE,{"disambiguationData":[OSD([sQuery(id+"F38.wireOp",EDGE,"E45")])],"isStart":false})});
            var Q6;
            {var subQ0=sQuery(id+"F38.wireOp",EDGE,"E43");var subQ1=sQuery(id+"F38.wireOp",EDGE,"E42");var subQ2=sQuery(id+"F32.wireOp",EDGE,"E38");var subQ3=makeQuery(id+"F38.imprint","INTERSECT",VERTEX,{"disambiguationData":[OD(0.0)],"derivedFrom":[makeQuery(id+"F37.opExtrude","CAP_EDGE",EDGE,{"disambiguationData":[OSD([sQuery(id+"F36.wireOp",EDGE,"E39")])],"isStart":true}),subQ0]});var subQ4=makeQuery(id+"F38.imprint","IMPRINT",EDGE,{"disambiguationData":[TD([[subQ3,-1.0]])],"derivedFrom":subQ0});var subQ5=makeQuery(id+"F38.imprint","IMPRINT",EDGE,{"disambiguationData":[TD([[makeQuery(id+"F38.imprint","INTERSECT",VERTEX,{"derivedFrom":[subQ1,subQ0]}),-1.0]])],"derivedFrom":subQ0});Q6=makeQuery(id+"F39.boolean.opBoolean","COPY",EDGE,{"disambiguationData":[TD([makeQuery(id+"F34.boolean.opBoolean","COPY",FACE,{"derivedFrom":makeQuery(id+"F34.opExtrude","SWEPT_FACE",FACE,{"disambiguationData":[OSD([sQuery(id+"F32.wireOp",EDGE,"E37")])]})}),makeQuery(id+"F35.boolean.opBoolean","COPY",FACE,{"derivedFrom":makeQuery(id+"F35.opExtrude","SWEPT_FACE",FACE,{"disambiguationData":[OSD([subQ2])]})}),makeQuery(id+"F39.opExtrude","CAP_FACE",FACE,{"disambiguationData":[OSD([subQ2,sQuery(id+"F38.wireOp",EDGE,"E41"),subQ1,subQ0])],"isStart":false}),makeQuery(id+"F39.opExtrude","SWEPT_FACE",FACE,{"disambiguationData":[OSD([subQ0]),TDD([subQ5,subQ4])]})])],"derivedFrom":makeQuery(id+"F39.opExtrude","CAP_EDGE",EDGE,{"disambiguationData":[OSD([subQ0]),TDD([subQ5,subQ4])],"isStart":false})});}
            var Q7;
            {var subQ0=sQuery(id+"F38.wireOp",EDGE,"E43");Q7=makeQuery(id+"F39.boolean.opBoolean","COPY",EDGE,{"derivedFrom":makeQuery(id+"F39.opExtrude","CAP_EDGE",EDGE,{"disambiguationData":[OSD([subQ0]),TDD([makeQuery(id+"F38.imprint","IMPRINT",EDGE,{"disambiguationData":[TD([[makeQuery(id+"F38.imprint","INTERSECT",VERTEX,{"disambiguationData":[OD(1.0)],"derivedFrom":[makeQuery(id+"F37.opExtrude","CAP_EDGE",EDGE,{"disambiguationData":[OSD([sQuery(id+"F36.wireOp",EDGE,"E39")])],"isStart":true}),subQ0]}),1.0]])],"derivedFrom":subQ0})])],"isStart":false})});}
            fillet(context, id + "F40", {"entities" : qUnion([Q0, Q1, Q2, Q3, Q4, Q5, Q6, Q7]), "radius" : 1 * mm, "tangentPropagation" : true, "rho" : .6, "crossSection" : FilletCrossSection.CONIC, "allowEdgeOverflow" : false});
        }
        {
            var Q0;
            Q0=makeQuery(id+"F33.boolean.opBoolean","MERGE",FACE,{"derivedFrom":[makeQuery(id+"F28.boolean.opBoolean","MERGE",FACE,{"derivedFrom":[makeQuery(id+"F1.opExtrude","SWEPT_FACE",FACE,{"disambiguationData":[OSD([sQuery(id+"F0.wireOp",EDGE,"E2")])]}),makeQuery(id+"F28.opExtrude","CAP_FACE",FACE,{"disambiguationData":[OSD([sQuery(id+"F8.wireOp",EDGE,"E17"),sQuery(id+"F27.wireOp",EDGE,"E32")])],"isStart":false})]}),makeQuery(id+"F33.opExtrude","CAP_FACE",FACE,{"disambiguationData":[OSD([sQuery(id+"F8.wireOp",EDGE,"E16"),sQuery(id+"F32.wireOp",EDGE,"E36")])],"isStart":false})]});
            var sketch = newSketch(context, id + "F41", { "sketchPlane" : qUnion([Q0])});
            skLineSegment(sketch, "E46", {"start": v(-20.7, 4) * mm, "end": v(-20.7, 4.5) * mm});
            skLineSegment(sketch, "E47", {"start": v(-20.7, 4.5) * mm, "end": v(-15.16, 4.5) * mm});
            skLineSegment(sketch, "E48", {"start": v(-15.16, 4.5) * mm, "end": v(-15.16, 3.5) * mm});
            skLineSegment(sketch, "E49", {"start": v(-15.16, 3.5) * mm, "end": v(-25, 3.5) * mm});
            skLineSegment(sketch, "E50", {"start": v(-25, 3.5) * mm, "end": v(-25, 4.5) * mm});
            skLineSegment(sketch, "E51", {"start": v(-25, 4.5) * mm, "end": v(-20.7, 4.5) * mm});
            skSolve(sketch);
        }
        {
            var Q0;
            {var subQ0=sQuery(id+"F41.wireOp",EDGE,"E47");var subQ1=makeQuery(id+"F5.boolean.opBoolean","COPY",EDGE,{"derivedFrom":makeQuery(id+"F5.opExtrude","CAP_EDGE",EDGE,{"disambiguationData":[OSD([sQuery(id+"F2.wireOp",EDGE,"E13")])],"isStart":true})});var subQ2=makeQuery(id+"F41.imprint","INTERSECT",VERTEX,{"derivedFrom":[subQ1,subQ0]});Q0=makeQuery(id+"F41.imprint","IMPRINT",FACE,{"disambiguationData":[TD([[makeQuery(id+"F41.imprint","IMPRINT",EDGE,{"disambiguationData":[TD([[subQ2,-1.0]])],"derivedFrom":subQ0}),-1.0]])]});}
            var Q1;
            {var subQ0=sQuery(id+"F41.wireOp",EDGE,"E50");Q1=makeQuery(id+"F41.imprint","IMPRINT",FACE,{"disambiguationData":[TD([[makeQuery(id+"F41.imprint","IMPRINT",EDGE,{"derivedFrom":subQ0}),-1.0]])]});}
            extrude(context, id + "F42", {"entities" : qUnion([Q0, Q1]), "operationType" : NewBodyOperationType.ADD, "oppositeDirection" : true, "depth" : 8 * mm, "offsetDistance" : 25 * mm});
        }
        {
            var Q0;
            Q0=makeQuery(id+"F1.opExtrude","CAP_FACE",FACE,{"disambiguationData":[OSD([sQuery(id+"F0.wireOp",EDGE,"E0"),sQuery(id+"F0.wireOp",EDGE,"E1"),sQuery(id+"F0.wireOp",EDGE,"E2"),sQuery(id+"F0.wireOp",EDGE,"E3"),sQuery(id+"F0.wireOp",EDGE,"E4"),sQuery(id+"F0.wireOp",EDGE,"E5"),sQuery(id+"F0.wireOp",EDGE,"E6.trimOffspring"),sQuery(id+"F0.wireOp",EDGE,"E7.trimOffspring"),sQuery(id+"F0.wireOp",EDGE,"E8.filletArc"),sQuery(id+"F0.wireOp",EDGE,"E9.filletArc"),sQuery(id+"F0.wireOp",EDGE,"E10.filletArc"),sQuery(id+"F0.wireOp",EDGE,"E11.filletArc")])],"isStart":false});
            var sketch = newSketch(context, id + "F43", { "sketchPlane" : qUnion([Q0])});
            skCircle(sketch, "E52", {"center": v(-28.2, -21.48) * mm, "radius": 3 * mm});
            skCircle(sketch, "E53", {"center": v(-28.2, -21.48) * mm, "radius": 2.5 * mm});
            skCircle(sketch, "E54", {"center": v(-28.2, -21.48) * mm, "radius": 4 * mm});
            skCircle(sketch, "E55", {"center": v(-13.2, -21.48) * mm, "radius": 3 * mm});
            skCircle(sketch, "E56", {"center": v(-13.2, -21.48) * mm, "radius": 4 * mm});
            skCircle(sketch, "E57", {"center": v(-13.2, -21.48) * mm, "radius": 2.5 * mm});
            skSolve(sketch);
        }
        {
            var Q0;
            Q0=makeQuery(id+"F43.imprint","IMPRINT",FACE,{"disambiguationData":[TD([[makeQuery(id+"F43.imprint","IMPRINT",EDGE,{"derivedFrom":sQuery(id+"F43.wireOp",EDGE,"E52")}),-1.0]])]});
            var Q1;
            Q1=makeQuery(id+"F43.imprint","IMPRINT",FACE,{"disambiguationData":[TD([[makeQuery(id+"F43.imprint","IMPRINT",EDGE,{"derivedFrom":sQuery(id+"F43.wireOp",EDGE,"E55")}),-1.0]])]});
            extrude(context, id + "F44", {"entities" : qUnion([Q0, Q1]), "operationType" : NewBodyOperationType.ADD, "depth" : .25 * mm, "offsetDistance" : 25 * mm});
        }
        {
            var Q0;
            Q0=makeQuery(id+"F43.imprint","IMPRINT",FACE,{"disambiguationData":[TD([[makeQuery(id+"F43.imprint","IMPRINT",EDGE,{"derivedFrom":sQuery(id+"F43.wireOp",EDGE,"E52")}),1.0]])]});
            var Q1;
            Q1=makeQuery(id+"F43.imprint","IMPRINT",FACE,{"disambiguationData":[TD([[makeQuery(id+"F43.imprint","IMPRINT",EDGE,{"derivedFrom":sQuery(id+"F43.wireOp",EDGE,"E55")}),1.0]])]});
            extrude(context, id + "F45", {"entities" : qUnion([Q0, Q1]), "operationType" : NewBodyOperationType.REMOVE, "oppositeDirection" : true, "depth" : .75 * mm, "offsetDistance" : 25 * mm});
        }
        {
            var Q0;
            Q0=makeQuery(id+"F43.imprint","IMPRINT",FACE,{"disambiguationData":[TD([[makeQuery(id+"F43.imprint","IMPRINT",EDGE,{"derivedFrom":sQuery(id+"F43.wireOp",EDGE,"E53")}),1.0]])]});
            var Q1;
            Q1=makeQuery(id+"F43.imprint","IMPRINT",FACE,{"disambiguationData":[TD([[makeQuery(id+"F43.imprint","IMPRINT",EDGE,{"derivedFrom":sQuery(id+"F43.wireOp",EDGE,"E57")}),1.0]])]});
            extrude(context, id + "F46", {"entities" : qUnion([Q0, Q1]), "operationType" : NewBodyOperationType.REMOVE, "oppositeDirection" : true, "depth" : 25 * mm, "offsetDistance" : 25 * mm});
        }
        {
            var Q0;
            Q0=makeQuery(id+"F1.opExtrude","CAP_FACE",FACE,{"disambiguationData":[OSD([sQuery(id+"F0.wireOp",EDGE,"E0"),sQuery(id+"F0.wireOp",EDGE,"E1"),sQuery(id+"F0.wireOp",EDGE,"E2"),sQuery(id+"F0.wireOp",EDGE,"E3"),sQuery(id+"F0.wireOp",EDGE,"E4"),sQuery(id+"F0.wireOp",EDGE,"E5"),sQuery(id+"F0.wireOp",EDGE,"E6.trimOffspring"),sQuery(id+"F0.wireOp",EDGE,"E7.trimOffspring"),sQuery(id+"F0.wireOp",EDGE,"E8.filletArc"),sQuery(id+"F0.wireOp",EDGE,"E9.filletArc"),sQuery(id+"F0.wireOp",EDGE,"E10.filletArc"),sQuery(id+"F0.wireOp",EDGE,"E11.filletArc")])],"isStart":true});
            var sketch = newSketch(context, id + "F47", { "sketchPlane" : qUnion([Q0])});
            skCircle(sketch, "E58", {"center": v(-28.2, 21.48) * mm, "radius": 4 * mm});
            skCircle(sketch, "E59", {"center": v(-28.2, 21.48) * mm, "radius": 3 * mm});
            skCircle(sketch, "E60", {"center": v(-13.2, 21.48) * mm, "radius": 4 * mm});
            skCircle(sketch, "E61", {"center": v(-13.2, 21.48) * mm, "radius": 3 * mm});
            skSolve(sketch);
        }
        {
            var Q0;
            Q0=makeQuery(id+"F47.imprint","IMPRINT",FACE,{"disambiguationData":[TD([[makeQuery(id+"F47.imprint","IMPRINT",EDGE,{"derivedFrom":sQuery(id+"F47.wireOp",EDGE,"E61")}),-1.0]])]});
            var Q1;
            Q1=makeQuery(id+"F47.imprint","IMPRINT",FACE,{"disambiguationData":[TD([[makeQuery(id+"F47.imprint","IMPRINT",EDGE,{"derivedFrom":sQuery(id+"F47.wireOp",EDGE,"E59")}),-1.0]])]});
            extrude(context, id + "F48", {"entities" : qUnion([Q0, Q1]), "operationType" : NewBodyOperationType.ADD, "depth" : .25 * mm, "offsetDistance" : 25 * mm});
        }
        {
            var Q0;
            Q0=makeQuery(id+"F48.boolean.opBoolean","SPLIT",FACE,{"disambiguationData":[TD([makeQuery(id+"F46.boolean.opBoolean","COPY",FACE,{"derivedFrom":makeQuery(id+"F46.opExtrude","SWEPT_FACE",FACE,{"disambiguationData":[OSD([sQuery(id+"F43.wireOp",EDGE,"E57")])]})})])],"derivedFrom":makeQuery(id+"F1.opExtrude","CAP_FACE",FACE,{"disambiguationData":[OSD([sQuery(id+"F0.wireOp",EDGE,"E0"),sQuery(id+"F0.wireOp",EDGE,"E1"),sQuery(id+"F0.wireOp",EDGE,"E2"),sQuery(id+"F0.wireOp",EDGE,"E3"),sQuery(id+"F0.wireOp",EDGE,"E4"),sQuery(id+"F0.wireOp",EDGE,"E5"),sQuery(id+"F0.wireOp",EDGE,"E6.trimOffspring"),sQuery(id+"F0.wireOp",EDGE,"E7.trimOffspring"),sQuery(id+"F0.wireOp",EDGE,"E8.filletArc"),sQuery(id+"F0.wireOp",EDGE,"E9.filletArc"),sQuery(id+"F0.wireOp",EDGE,"E10.filletArc"),sQuery(id+"F0.wireOp",EDGE,"E11.filletArc")])],"isStart":true})});
            var Q1;
            Q1=makeQuery(id+"F48.boolean.opBoolean","SPLIT",FACE,{"disambiguationData":[TD([makeQuery(id+"F46.boolean.opBoolean","COPY",FACE,{"derivedFrom":makeQuery(id+"F46.opExtrude","SWEPT_FACE",FACE,{"disambiguationData":[OSD([sQuery(id+"F43.wireOp",EDGE,"E53")])]})})])],"derivedFrom":makeQuery(id+"F1.opExtrude","CAP_FACE",FACE,{"disambiguationData":[OSD([sQuery(id+"F0.wireOp",EDGE,"E0"),sQuery(id+"F0.wireOp",EDGE,"E1"),sQuery(id+"F0.wireOp",EDGE,"E2"),sQuery(id+"F0.wireOp",EDGE,"E3"),sQuery(id+"F0.wireOp",EDGE,"E4"),sQuery(id+"F0.wireOp",EDGE,"E5"),sQuery(id+"F0.wireOp",EDGE,"E6.trimOffspring"),sQuery(id+"F0.wireOp",EDGE,"E7.trimOffspring"),sQuery(id+"F0.wireOp",EDGE,"E8.filletArc"),sQuery(id+"F0.wireOp",EDGE,"E9.filletArc"),sQuery(id+"F0.wireOp",EDGE,"E10.filletArc"),sQuery(id+"F0.wireOp",EDGE,"E11.filletArc")])],"isStart":true})});
            extrude(context, id + "F49", {"entities" : qUnion([Q0, Q1]), "operationType" : NewBodyOperationType.REMOVE, "oppositeDirection" : true, "depth" : .75 * mm, "offsetDistance" : 25 * mm});
        }
    });
